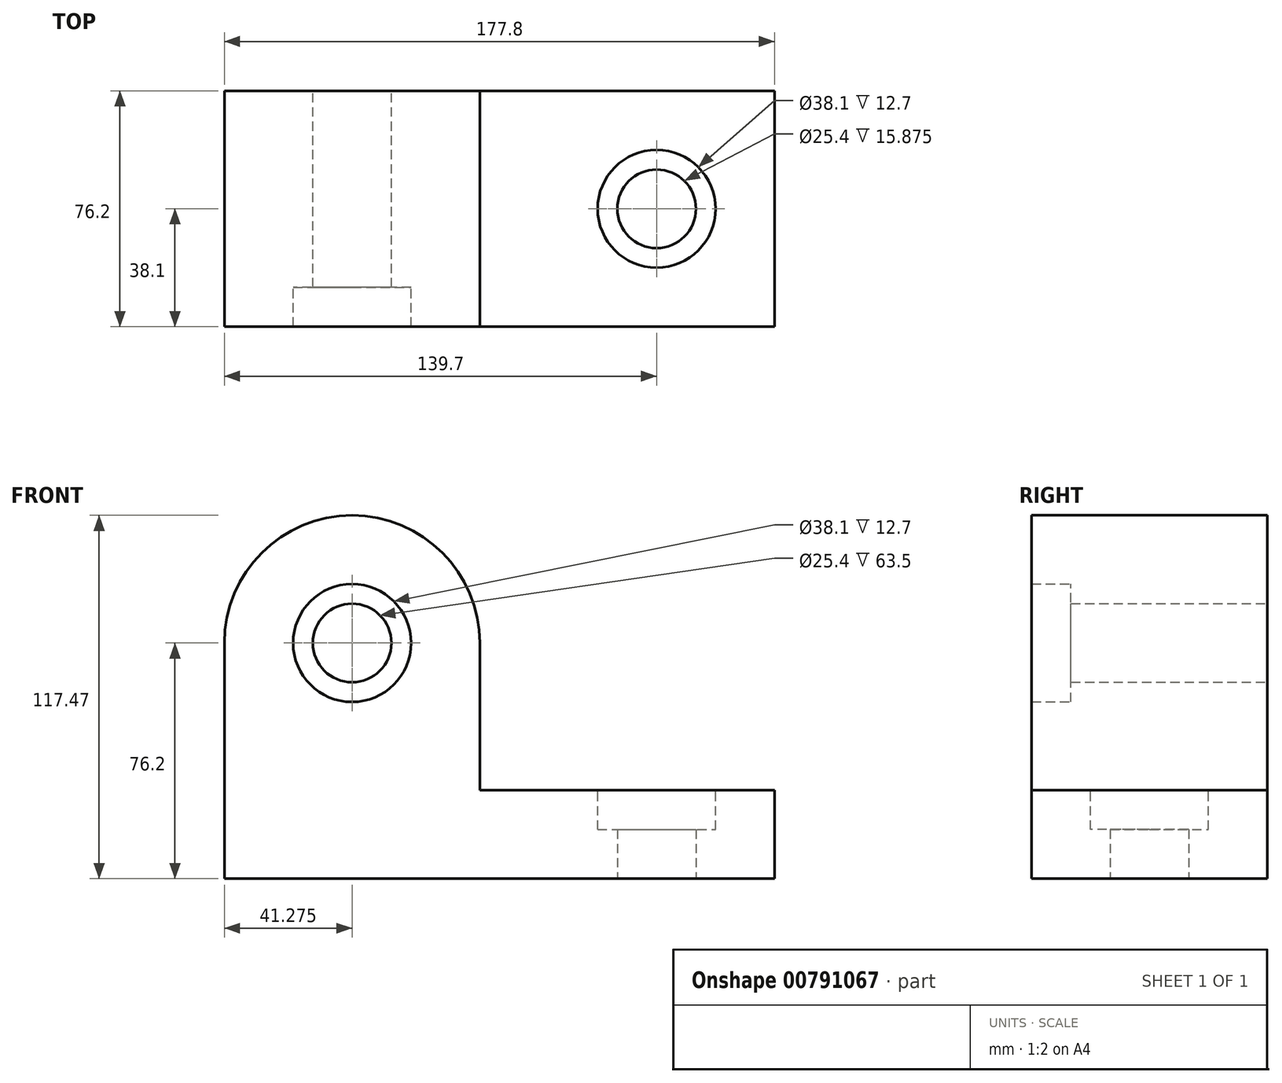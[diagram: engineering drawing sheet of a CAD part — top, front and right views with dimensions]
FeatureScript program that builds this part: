
annotation { "Feature Type Name" : "Feature", "Feature Type Description" : "" }
export const myFeature = defineFeature(function(context is Context, id is Id, definition is map)
    precondition{}
    {
        {
            var Q0;
            Q0=qCreatedBy(makeId("Front.planeOp"),FACE);
            var sketch = newSketch(context, id + "F0", { "sketchPlane" : qUnion([Q0])});
            skLineSegment(sketch, "E0", {"start": v(0, 0) * mm, "end": v(177.8, 0) * mm});
            skLineSegment(sketch, "E1", {"start": v(177.8, 0) * mm, "end": v(177.8, 28.57) * mm});
            skLineSegment(sketch, "E2", {"start": v(0, 0) * mm, "end": v(0, 76.2) * mm});
            skLineSegment(sketch, "E3", {"start": v(0, 76.2) * mm, "end": v(82.55, 76.2) * mm});
            skLineSegment(sketch, "E4", {"start": v(82.55, 76.2) * mm, "end": v(82.55, 28.57) * mm});
            skLineSegment(sketch, "E5", {"start": v(82.55, 28.57) * mm, "end": v(177.8, 28.57) * mm});
            skArc(sketch, "E6", {"start": v(0, 76.2) * mm, "mid": v(41.28, 117.48) * mm, "end": v(82.55, 76.2) * mm});
            skCircle(sketch, "E7", {"center": v(41.28, 76.2) * mm, "radius": 19.05 * mm});
            skCircle(sketch, "E8", {"center": v(41.28, 76.2) * mm, "radius": 12.7 * mm});
            skSolve(sketch);
        }
        {
            var Q0;
            Q0 = qSketchRegion(id + "F0", true);
            extrude(context, id + "F1", {"entities" : qUnion([Q0]), "depth" : 76.2 * mm, "offsetDistance" : 25.4 * mm});
        }
        {
            var Q0;
            {var subQ0=sQuery(id+"F0.wireOp",EDGE,"E7");var subQ1=sQuery(id+"F0.wireOp",EDGE,"E3");var subQ2=makeQuery(id+"F0.imprint","INTERSECT",VERTEX,{"disambiguationData":[OD(0.0)],"derivedFrom":[subQ1,subQ0]});Q0=makeQuery(id+"F0.imprint","IMPRINT",FACE,{"disambiguationData":[TD([[makeQuery(id+"F0.imprint","IMPRINT",EDGE,{"disambiguationData":[TD([[subQ2,-1.0]])],"derivedFrom":subQ1}),-1.0]])]});}
            var Q1;
            {var subQ0=sQuery(id+"F0.wireOp",EDGE,"E7");var subQ1=sQuery(id+"F0.wireOp",EDGE,"E3");var subQ2=makeQuery(id+"F0.imprint","INTERSECT",VERTEX,{"disambiguationData":[OD(0.0)],"derivedFrom":[subQ1,subQ0]});Q1=makeQuery(id+"F0.imprint","IMPRINT",FACE,{"disambiguationData":[TD([[makeQuery(id+"F0.imprint","IMPRINT",EDGE,{"disambiguationData":[TD([[subQ2,-1.0]])],"derivedFrom":subQ1}),1.0]])]});}
            extrude(context, id + "F2", {"entities" : qUnion([Q0, Q1]), "operationType" : NewBodyOperationType.ADD, "depth" : 63.5 * mm, "offsetDistance" : 25.4 * mm});
        }
        {
            var Q0;
            Q0=makeQuery(id+"F1.opExtrude","SWEPT_FACE",FACE,{"disambiguationData":[OSD([sQuery(id+"F0.wireOp",EDGE,"E5")])]});
            var sketch = newSketch(context, id + "F3", { "sketchPlane" : qUnion([Q0])});
            skLineSegment(sketch, "E9", {"start": v(177.8, -38.1) * mm, "end": v(139.7, -38.1) * mm, "construction": true});
            skCircle(sketch, "E10", {"center": v(139.7, -38.1) * mm, "radius": 19.05 * mm});
            skSolve(sketch);
        }
        {
            var Q0;
            Q0=makeQuery(id+"F3.imprint","IMPRINT",FACE,{"disambiguationData":[TD([[makeQuery(id+"F3.imprint","IMPRINT",EDGE,{"derivedFrom":sQuery(id+"F3.wireOp",EDGE,"E10")}),1.0]])]});
            extrude(context, id + "F4", {"entities" : qUnion([Q0]), "operationType" : NewBodyOperationType.REMOVE, "oppositeDirection" : true, "depth" : 127 * mm, "offsetDistance" : 25.4 * mm});
        }
        {
            var Q0;
            Q0=makeQuery(id+"F1.opExtrude","SWEPT_FACE",FACE,{"disambiguationData":[OSD([sQuery(id+"F0.wireOp",EDGE,"E0")])]});
            var sketch = newSketch(context, id + "F5", { "sketchPlane" : qUnion([Q0])});
            skLineSegment(sketch, "E11", {"start": v(177.8, 38.1) * mm, "end": v(139.7, 38.1) * mm});
            skLineSegment(sketch, "E12", {"start": v(139.7, 38.1) * mm, "end": v(120.65, 38.1) * mm});
            skCircle(sketch, "E13", {"center": v(139.7, 38.1) * mm, "radius": 19.05 * mm});
            skCircle(sketch, "E14", {"center": v(139.7, 38.1) * mm, "radius": 12.7 * mm});
            skSolve(sketch);
        }
        {
            var Q0;
            Q0 = qSketchRegion(id + "F5", true);
            extrude(context, id + "F6", {"entities" : qUnion([Q0]), "operationType" : NewBodyOperationType.ADD, "depth" : -15.88 * mm, "offsetDistance" : 25.4 * mm});
        }
    });
